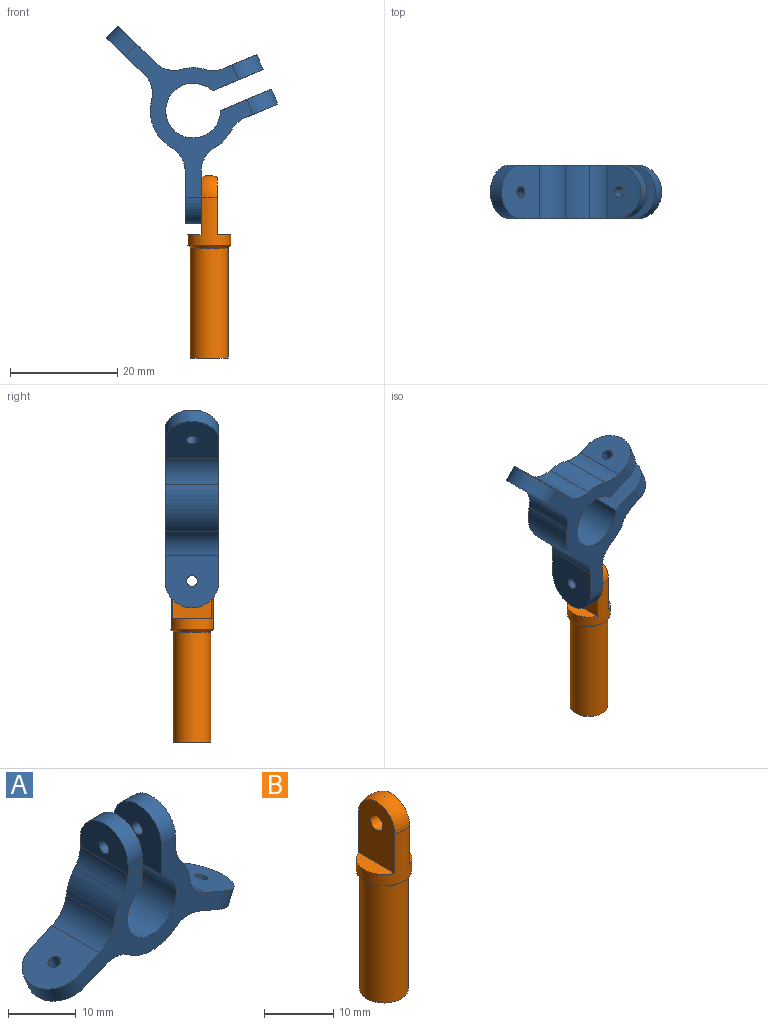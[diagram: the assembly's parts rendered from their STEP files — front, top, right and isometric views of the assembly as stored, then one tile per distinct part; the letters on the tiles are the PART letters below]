
ASSEMBLY  parts=2 mates=1
PART A: 28 faces, bbox 40x10x24.6 mm
  f0: cylinder r=5.1mm len=10.2mm, axis (0,1,0), area 279.3mm2, adj f6,f7,f8,f20
  f1: cylinder r=8mm len=10mm, axis (0,1,0), area 103.5mm2, adj f7,f8,f15,f27
  f2: plane 10x9.06mm, normal (-0.39,0,-0.92), area 84.5mm2, adj f7,f8,f9,f11,f15
  f3: plane 10x9.06mm, normal (0.39,0,0.92), area 84.5mm2, adj f7,f8,f9,f11,f13
  f4: cylinder r=8mm len=10mm, axis (0,1,0), area 45.6mm2, adj f7,f8,f13,f14
  f5: plane 10x6.69mm, normal (1,0,0), area 53.1mm2, adj f7,f8,f10,f12,f14
  f6: plane 10.31x10mm, normal (-1,0,0), area 89.2mm2, adj f0,f7,f8,f10,f12
  f7: plane 30.83x18mm, normal (0,-1,0), area 181.7mm2, adj f0,f1,f2,f3,f4,f5,f6,f11
  f8: plane 30.83x18mm, normal (0,1,0), area 181.7mm2, adj f0,f1,f2,f3,f4,f5,f6,f11
  f9: cylinder r=1mm len=3.54mm, axis (0.39,0,0.92), area 18.8mm2, adj f2,f3
  f10: cylinder r=1mm len=3mm, axis (1,0,0), area 18.8mm2, adj f5,f6
  f11: cylinder r=5mm len=10mm, axis (-0.39,0,-0.92), area 47.1mm2, adj f2,f3,f7,f8
  f12: cylinder r=5mm len=10mm, axis (1,0,0), area 47.1mm2, adj f5,f6,f7,f8
  f13: cylinder r=5mm len=10mm, axis (0,1,0), area 52.4mm2, adj f3,f4,f7,f8
  f14: cylinder r=5mm len=10mm, axis (0,1,0), area 34.7mm2, adj f4,f5,f7,f8
  f15: cylinder r=5mm len=10mm, axis (0,1,0), area 52.4mm2, adj f1,f2,f7,f8
  f16: plane 10x9.06mm, normal (0.39,0,-0.92), area 84.5mm2, adj f7,f8,f21,f23,f27
  f17: plane 10x9.06mm, normal (-0.39,0,0.92), area 84.5mm2, adj f7,f8,f21,f23,f25
  f18: cylinder r=8mm len=10mm, axis (0,1,0), area 45.6mm2, adj f7,f8,f25,f26
  f19: plane 10x6.69mm, normal (-1,0,0), area 53.1mm2, adj f7,f8,f22,f24,f26
  f20: plane 10.31x10mm, normal (1,0,0), area 89.2mm2, adj f0,f7,f8,f22,f24
  f21: cylinder r=1mm len=3.54mm, axis (-0.39,0,0.92), area 18.8mm2, adj f16,f17
  f22: cylinder r=1mm len=3mm, axis (-1,0,0), area 18.8mm2, adj f19,f20
  f23: cylinder r=5mm len=10mm, axis (0.39,0,-0.92), area 47.1mm2, adj f7,f8,f16,f17
  f24: cylinder r=5mm len=10mm, axis (-1,0,0), area 47.1mm2, adj f7,f8,f19,f20
  f25: cylinder r=5mm len=10mm, axis (0,1,0), area 52.4mm2, adj f7,f8,f17,f18
  f26: cylinder r=5mm len=10mm, axis (0,1,0), area 34.7mm2, adj f7,f8,f18,f19
  f27: cylinder r=5mm len=10mm, axis (0,1,0), area 52.4mm2, adj f1,f7,f8,f16
PART B: 13 faces, bbox 8x8x34 mm
  f0: cylinder r=4mm len=9mm, axis (0,0,1), area 93.3mm2, adj f1,f7,f8,f9,f10,f11
  f1: sphere r=4mm, area 37.7mm2, adj f0,f9,f11
  f2: plane 2x2mm, normal (0,0,-1), area 3.1mm2, adj f3
  f3: torus R=1mm, axis (0,0,1), area 16.2mm2, adj f2,f4
  f4: cylinder r=2mm len=17mm, axis (0,0,1), area 213.6mm2, adj f3,f5
  f5: plane 7x7mm, normal (0,0,-1), area 25.9mm2, adj f4,f6
  f6: cylinder r=3.5mm len=20.5mm, axis (0,0,1), area 450.8mm2, adj f5,f7
  f7: cone r=3.5mm half-angle=45deg, axis (0,0,1), area 16.7mm2, adj f0,f6
  f8: plane 7.42x2.5mm, normal (0,0,1), area 13.4mm2, adj f0,f9
  f9: plane 10.71x7.42mm, normal (-1,0,0), area 68.6mm2, adj f0,f1,f8,f12
  f10: plane 7.42x2.5mm, normal (0,0,1), area 13.4mm2, adj f0,f11
  f11: plane 10.71x7.42mm, normal (1,0,0), area 68.6mm2, adj f0,f1,f10,f12
  f12: cylinder r=1.25mm len=3mm, axis (-1,0,0), area 23.6mm2, adj f9,f11
PLACE A rot(axis=(0,1,0),67.1deg) t=(23.45,22.07,18.93)mm
PLACE B t=(26.45,22.07,-9.17)mm
MATE cylindrical A.f9 <-> B.f12  axis (1,0,0) through (24.95,22.07,2.83)mm
